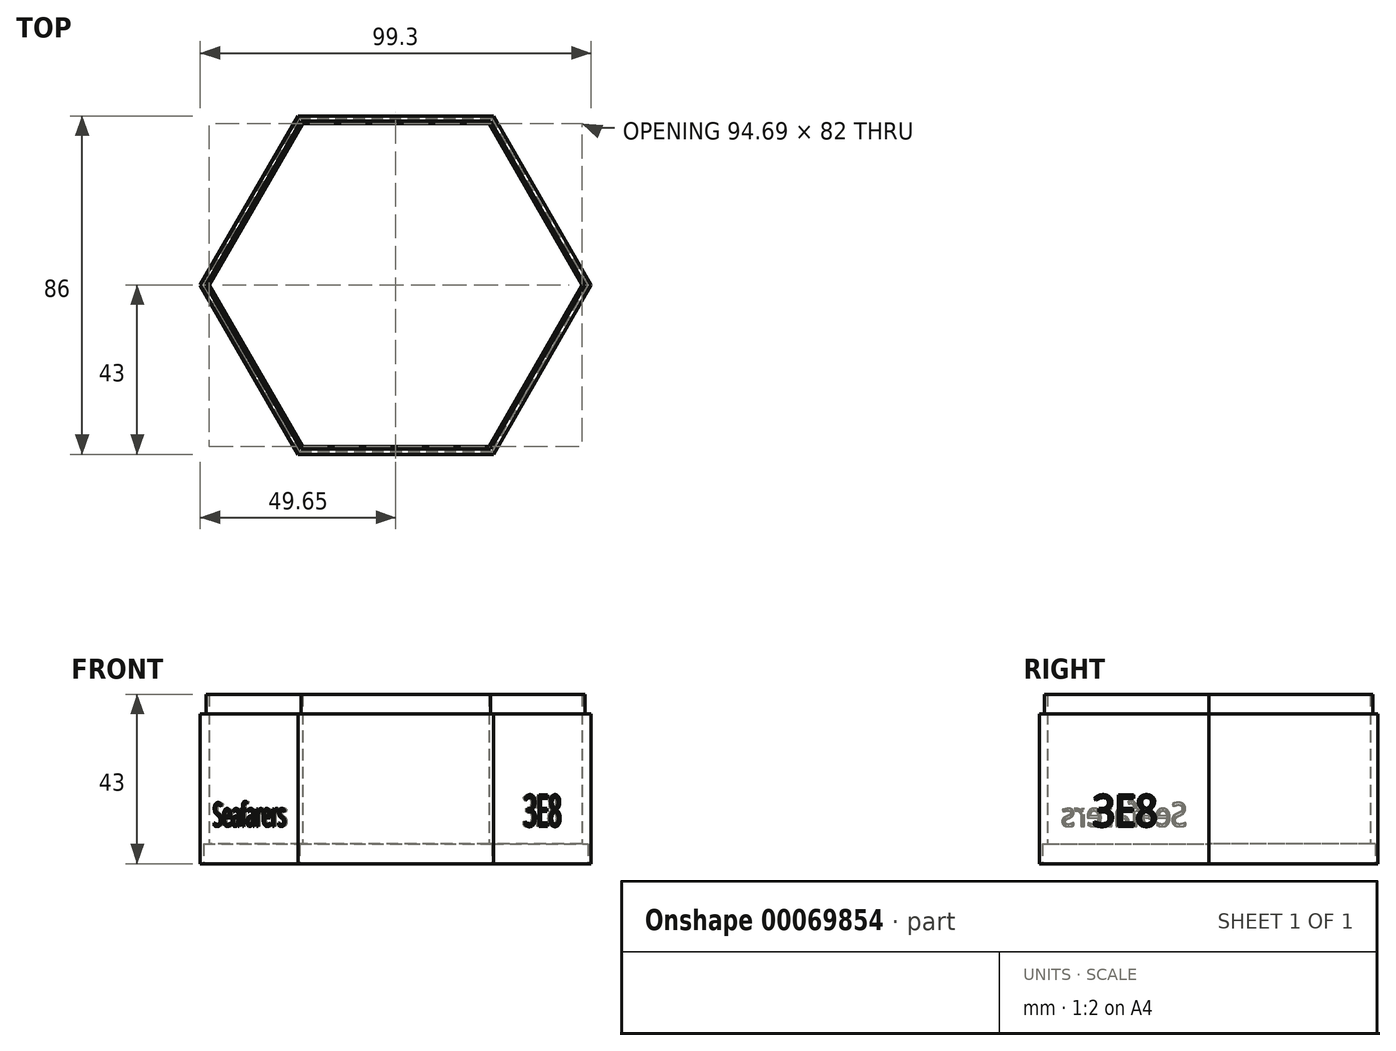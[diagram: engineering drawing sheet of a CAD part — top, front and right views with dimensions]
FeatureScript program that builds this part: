
annotation { "Feature Type Name" : "Feature", "Feature Type Description" : "" }
export const myFeature = defineFeature(function(context is Context, id is Id, definition is map)
    precondition{}
    {
        {
            var Q0;
            Q0=qCreatedBy(makeId("Top.planeOp"),FACE);
            var sketch = newSketch(context, id + "F0", { "sketchPlane" : qUnion([Q0])});
            skLineSegment(sketch, "E0.rect.bottom", {"start": v(24.83, -43) * mm, "end": v(-24.83, -43) * mm});
            skLineSegment(sketch, "E0.rect.top", {"start": v(24.83, 43) * mm, "end": v(-24.83, 43) * mm});
            skLineSegment(sketch, "E0.rect.left", {"start": v(24.83, -43) * mm, "end": v(24.83, 43) * mm, "construction": true});
            skLineSegment(sketch, "E0.rect.right", {"start": v(-24.83, -43) * mm, "end": v(-24.83, 43) * mm, "construction": true});
            skPoint(sketch, "E0.rect.middle", {"position": v(0, 0) * mm});
            skLineSegment(sketch, "E1", {"start": v(-49.65, 0) * mm, "end": v(-24.83, 43) * mm});
            skLineSegment(sketch, "E2", {"start": v(24.83, -43) * mm, "end": v(49.65, 0) * mm});
            skLineSegment(sketch, "E3", {"start": v(24.83, 43) * mm, "end": v(49.65, 0) * mm});
            skLineSegment(sketch, "E4", {"start": v(-49.65, 0) * mm, "end": v(-24.83, -43) * mm});
            skLineSegment(sketch, "E5", {"start": v(-37.24, -21.5) * mm, "end": v(37.24, 21.5) * mm, "construction": true});
            skSolve(sketch);
        }
        {
            var Q0;
            Q0=qSketchRegion(id+"F0",true);
            extrude(context, id + "F1", {"entities" : qUnion([Q0]), "depth" : 2 * mm});
        }
        {
            var Q0;
            Q0=makeQuery(id+"F1.opExtrude","CAP_FACE",FACE,{"disambiguationData":[OSD([sQuery(id+"F0.wireOp",EDGE,"E0.rect.bottom"),sQuery(id+"F0.wireOp",EDGE,"E0.rect.top"),sQuery(id+"F0.wireOp",EDGE,"E1"),sQuery(id+"F0.wireOp",EDGE,"E2"),sQuery(id+"F0.wireOp",EDGE,"E3"),sQuery(id+"F0.wireOp",EDGE,"E4")])],"isStart":false});
            var sketch = newSketch(context, id + "F2", { "sketchPlane" : qUnion([Q0])});
            skLineSegment(sketch, "E6.0.0", {"start": v(-24.83, -43) * mm, "end": v(24.83, -43) * mm});
            skLineSegment(sketch, "E6.0.1", {"start": v(24.83, -43) * mm, "end": v(49.65, 0) * mm});
            skLineSegment(sketch, "E6.0.2", {"start": v(49.65, 0) * mm, "end": v(24.83, 43) * mm});
            skLineSegment(sketch, "E6.0.3", {"start": v(24.83, 43) * mm, "end": v(-24.83, 43) * mm});
            skLineSegment(sketch, "E6.0.4", {"start": v(-24.83, 43) * mm, "end": v(-49.65, 0) * mm});
            skLineSegment(sketch, "E6.0.5", {"start": v(-49.65, 0) * mm, "end": v(-24.83, -43) * mm});
            skLineSegment(sketch, "E7.0", {"start": v(23.67, 41) * mm, "end": v(-23.67, 41) * mm});
            skLineSegment(sketch, "E7.1", {"start": v(-47.34, 0) * mm, "end": v(-23.67, -41) * mm});
            skLineSegment(sketch, "E7.2", {"start": v(-23.67, -41) * mm, "end": v(23.67, -41) * mm});
            skLineSegment(sketch, "E7.3", {"start": v(-23.67, 41) * mm, "end": v(-47.34, 0) * mm});
            skLineSegment(sketch, "E7.4", {"start": v(23.67, -41) * mm, "end": v(47.34, 0) * mm});
            skLineSegment(sketch, "E7.5", {"start": v(47.34, 0) * mm, "end": v(23.67, 41) * mm});
            skSolve(sketch);
        }
        {
            var Q0;
            Q0=qSketchRegion(id+"F2",true);
            extrude(context, id + "F3", {"entities" : qUnion([Q0]), "operationType" : NewBodyOperationType.ADD, "depth" : 41 * mm});
        }
        {
            var Q0;
            Q0=makeQuery(id+"F3.opExtrude","CAP_FACE",FACE,{"disambiguationData":[OSD([sQuery(id+"F2.wireOp",EDGE,"E6.0.0"),sQuery(id+"F2.wireOp",EDGE,"E6.0.1"),sQuery(id+"F2.wireOp",EDGE,"E6.0.2"),sQuery(id+"F2.wireOp",EDGE,"E6.0.3"),sQuery(id+"F2.wireOp",EDGE,"E6.0.4"),sQuery(id+"F2.wireOp",EDGE,"E6.0.5"),sQuery(id+"F2.wireOp",EDGE,"E7.0"),sQuery(id+"F2.wireOp",EDGE,"E7.1"),sQuery(id+"F2.wireOp",EDGE,"E7.2"),sQuery(id+"F2.wireOp",EDGE,"E7.3"),sQuery(id+"F2.wireOp",EDGE,"E7.4"),sQuery(id+"F2.wireOp",EDGE,"E7.5")])],"isStart":false});
            var sketch = newSketch(context, id + "F4", { "sketchPlane" : qUnion([Q0])});
            skLineSegment(sketch, "E8.0", {"start": v(-49.65, 0) * mm, "end": v(-24.83, 43) * mm});
            skLineSegment(sketch, "E9.0", {"start": v(24.83, 43) * mm, "end": v(-24.83, 43) * mm});
            skLineSegment(sketch, "E10.0", {"start": v(24.83, 43) * mm, "end": v(49.65, 0) * mm});
            skLineSegment(sketch, "E11.0", {"start": v(24.83, -43) * mm, "end": v(49.65, 0) * mm});
            skLineSegment(sketch, "E12.0", {"start": v(24.83, -43) * mm, "end": v(-24.83, -43) * mm});
            skLineSegment(sketch, "E13.0", {"start": v(-49.65, 0) * mm, "end": v(-24.83, -43) * mm});
            skLineSegment(sketch, "E14.0", {"start": v(-48.15, 0) * mm, "end": v(-24.08, -41.7) * mm});
            skLineSegment(sketch, "E14.1", {"start": v(24.08, 41.7) * mm, "end": v(-24.08, 41.7) * mm});
            skLineSegment(sketch, "E14.2", {"start": v(24.08, 41.7) * mm, "end": v(48.15, 0) * mm});
            skLineSegment(sketch, "E14.3", {"start": v(-48.15, 0) * mm, "end": v(-24.08, 41.7) * mm});
            skLineSegment(sketch, "E14.4", {"start": v(24.08, -41.7) * mm, "end": v(48.15, 0) * mm});
            skLineSegment(sketch, "E14.5", {"start": v(24.08, -41.7) * mm, "end": v(-24.08, -41.7) * mm});
            skSolve(sketch);
        }
        {
            var Q0;
            Q0=qSketchRegion(id+"F4",true);
            extrude(context, id + "F5", {"entities" : qUnion([Q0]), "operationType" : NewBodyOperationType.REMOVE, "oppositeDirection" : true, "depth" : 5 * mm});
        }
        {
            var Q0;
            Q0=makeQuery(id+"F3.boolean.opBoolean","MERGE",FACE,{"derivedFrom":[makeQuery(id+"F1.opExtrude","SWEPT_FACE",FACE,{"disambiguationData":[OSD([sQuery(id+"F0.wireOp",EDGE,"E2")])]}),makeQuery(id+"F3.opExtrude","SWEPT_FACE",FACE,{"disambiguationData":[OSD([sQuery(id+"F2.wireOp",EDGE,"E6.0.1")])]})]});
            var sketch = newSketch(context, id + "F6", { "sketchPlane" : qUnion([Q0])});
            skText(sketch, "E15", { "text": "3E8", "fontName": "OpenSans-Regular.ttf"});
            skLineSegment(sketch, "E16", {"start": v(24.83, 38) * mm, "end": v(-24.83, 0) * mm, "construction": true});
            skPoint(sketch, "E17", {"position": v(0, 19) * mm});
            skPoint(sketch, "E17.positionSnap0", {"position": v(9.17, 19) * mm});
            const initialGuessF6  = {"E15": [-0.00917, 0.0095, 1, 0, 0.008]};
            skSetInitialGuess(sketch, initialGuessF6);
            skSolve(sketch);
        }
        {
            var Q0;
            Q0=qSketchRegion(id+"F6",true);
            extrude(context, id + "F7", {"entities" : qUnion([Q0]), "operationType" : NewBodyOperationType.REMOVE, "oppositeDirection" : true, "depth" : .5 * mm});
        }
        {
            var Q0;
            Q0=makeQuery(id+"F1.opExtrude","CAP_FACE",FACE,{"disambiguationData":[OSD([sQuery(id+"F0.wireOp",EDGE,"E0.rect.bottom"),sQuery(id+"F0.wireOp",EDGE,"E0.rect.top"),sQuery(id+"F0.wireOp",EDGE,"E1"),sQuery(id+"F0.wireOp",EDGE,"E2"),sQuery(id+"F0.wireOp",EDGE,"E3"),sQuery(id+"F0.wireOp",EDGE,"E4")])],"isStart":false});
            extrude(context, id + "F8", {"entities" : qUnion([Q0]), "operationType" : NewBodyOperationType.REMOVE, "endBound" : BoundingType.THROUGH_ALL, "oppositeDirection" : true, "depth" : 25 * mm});
        }
        {
            var Q0;
            Q0=makeQuery(id+"F1.opExtrude","CAP_FACE",FACE,{"disambiguationData":[OSD([sQuery(id+"F0.wireOp",EDGE,"E0.rect.bottom"),sQuery(id+"F0.wireOp",EDGE,"E0.rect.top"),sQuery(id+"F0.wireOp",EDGE,"E1"),sQuery(id+"F0.wireOp",EDGE,"E2"),sQuery(id+"F0.wireOp",EDGE,"E3"),sQuery(id+"F0.wireOp",EDGE,"E4")])],"isStart":true});
            var sketch = newSketch(context, id + "F9", { "sketchPlane" : qUnion([Q0])});
            skLineSegment(sketch, "E18.0", {"start": v(23.67, 41) * mm, "end": v(47.34, 0) * mm});
            skLineSegment(sketch, "E19.0", {"start": v(47.34, 0) * mm, "end": v(23.67, -41) * mm});
            skLineSegment(sketch, "E20.0", {"start": v(-23.67, 41) * mm, "end": v(23.67, 41) * mm});
            skLineSegment(sketch, "E21.0", {"start": v(-47.34, 0) * mm, "end": v(-23.67, 41) * mm});
            skLineSegment(sketch, "E22.0", {"start": v(-23.67, -41) * mm, "end": v(-47.34, 0) * mm});
            skLineSegment(sketch, "E23.0", {"start": v(23.67, -41) * mm, "end": v(-23.67, -41) * mm});
            skLineSegment(sketch, "E24.0", {"start": v(-24.42, 42.3) * mm, "end": v(24.42, 42.3) * mm});
            skLineSegment(sketch, "E24.1", {"start": v(48.84, 0) * mm, "end": v(24.42, -42.3) * mm});
            skLineSegment(sketch, "E24.2", {"start": v(24.42, -42.3) * mm, "end": v(-24.42, -42.3) * mm});
            skLineSegment(sketch, "E24.3", {"start": v(24.42, 42.3) * mm, "end": v(48.84, 0) * mm});
            skLineSegment(sketch, "E24.4", {"start": v(-24.42, -42.3) * mm, "end": v(-48.84, 0) * mm});
            skLineSegment(sketch, "E24.5", {"start": v(-48.84, 0) * mm, "end": v(-24.42, 42.3) * mm});
            skSolve(sketch);
        }
        {
            var Q0;
            Q0 = qSketchRegion(id + "F9", true);
            extrude(context, id + "F10", {"entities" : qUnion([Q0]), "operationType" : NewBodyOperationType.REMOVE, "oppositeDirection" : true, "depth" : 5 * mm});
        }
        {
            var Q0;
            Q0=makeQuery(id+"F3.boolean.opBoolean","MERGE",FACE,{"derivedFrom":[makeQuery(id+"F1.opExtrude","SWEPT_FACE",FACE,{"disambiguationData":[OSD([sQuery(id+"F0.wireOp",EDGE,"E4")])]}),makeQuery(id+"F3.opExtrude","SWEPT_FACE",FACE,{"disambiguationData":[OSD([sQuery(id+"F2.wireOp",EDGE,"E6.0.5")])]})]});
            var sketch = newSketch(context, id + "F11", { "sketchPlane" : qUnion([Q0])});
            skText(sketch, "E25", { "text": "Seafarers", "fontName": "OpenSans-Regular.ttf"});
            skLineSegment(sketch, "E26", {"start": v(24.83, 38) * mm, "end": v(-24.83, 0) * mm, "construction": true});
            skPoint(sketch, "E27", {"position": v(0, 19) * mm});
            const initialGuessF11  = {"E25": [-0.0182, 0.0095, 1, 0, 0.006]};
            skSetInitialGuess(sketch, initialGuessF11);
            skSolve(sketch);
        }
        {
            var Q0;
            Q0 = qSketchRegion(id + "F11", true);
            extrude(context, id + "F12", {"entities" : qUnion([Q0]), "operationType" : NewBodyOperationType.REMOVE, "oppositeDirection" : true, "depth" : .5 * mm});
        }
    });
